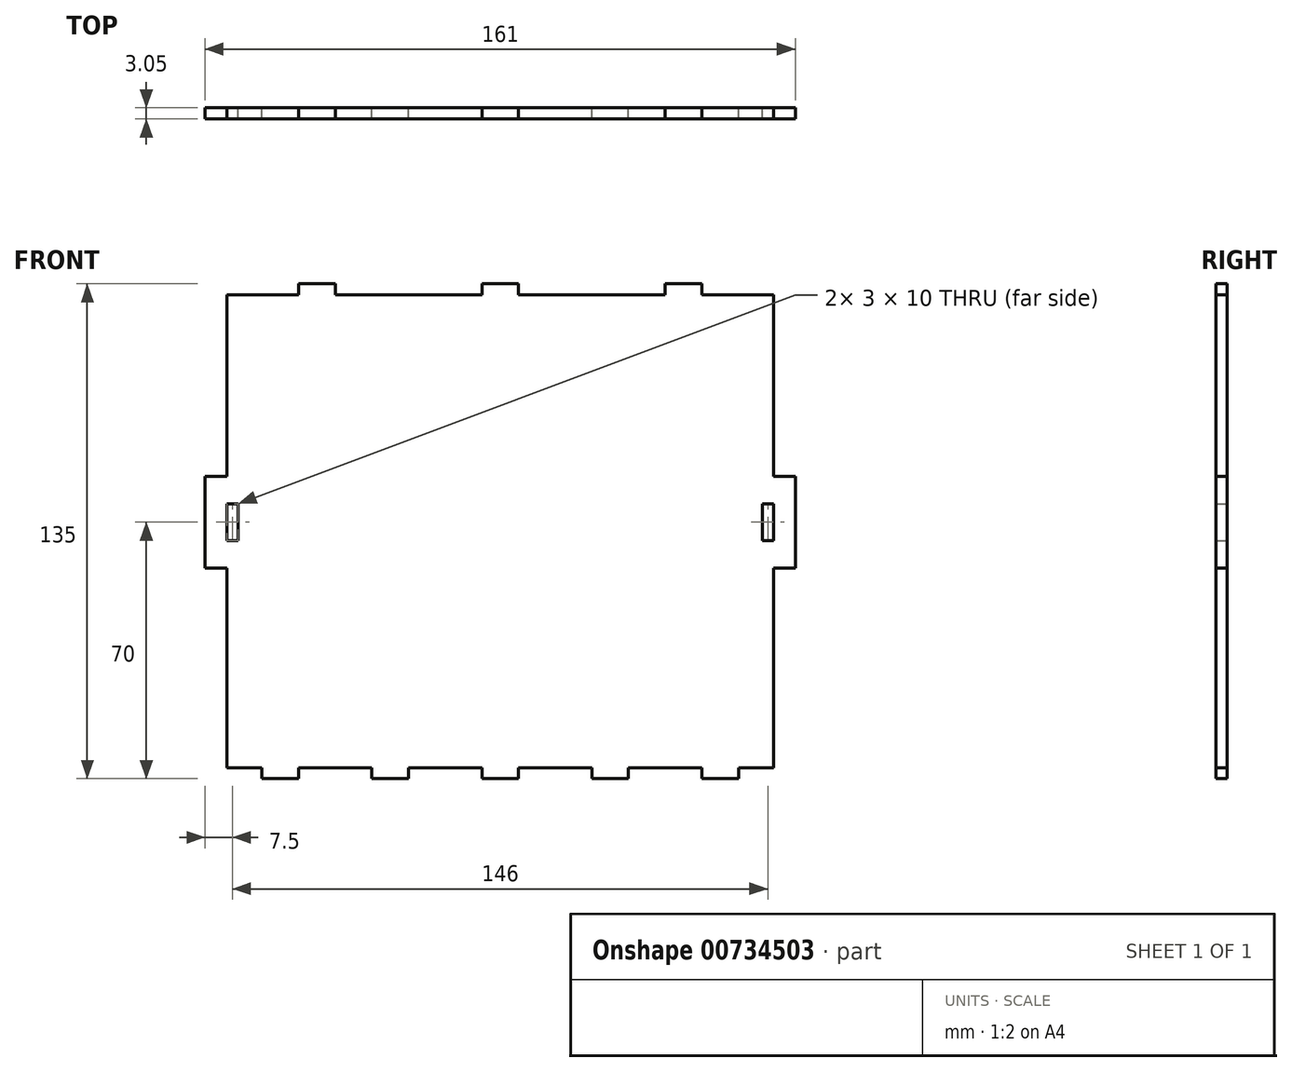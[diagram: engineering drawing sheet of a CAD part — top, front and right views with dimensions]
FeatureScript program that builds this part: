
annotation { "Feature Type Name" : "Feature", "Feature Type Description" : "" }
export const myFeature = defineFeature(function(context is Context, id is Id, definition is map)
    precondition{}
    {
        {
            var Q0;
            Q0=qCreatedBy(makeId("Front.planeOp"),FACE);
            var sketch = newSketch(context, id + "F0", { "sketchPlane" : qUnion([Q0])});
            skLineSegment(sketch, "E0", {"start": v(74.5, 7.5) * mm, "end": v(71.5, 7.5) * mm});
            skLineSegment(sketch, "E1", {"start": v(71.5, 7.5) * mm, "end": v(71.5, -2.5) * mm});
            skLineSegment(sketch, "E2", {"start": v(71.5, -2.5) * mm, "end": v(74.5, -2.5) * mm});
            skLineSegment(sketch, "E3", {"start": v(74.5, -2.5) * mm, "end": v(74.5, 7.5) * mm});
            skLineSegment(sketch, "E4", {"start": v(-74.5, -2.5) * mm, "end": v(-71.5, -2.5) * mm});
            skLineSegment(sketch, "E5", {"start": v(-71.5, -2.5) * mm, "end": v(-71.5, 7.5) * mm});
            skLineSegment(sketch, "E6", {"start": v(-71.5, 7.5) * mm, "end": v(-74.5, 7.5) * mm});
            skLineSegment(sketch, "E7", {"start": v(-74.5, 7.5) * mm, "end": v(-74.5, -2.5) * mm});
            skLineSegment(sketch, "E8", {"start": v(-74.5, 15) * mm, "end": v(-74.5, 64.5) * mm});
            skLineSegment(sketch, "E9", {"start": v(-74.5, 64.5) * mm, "end": v(-55, 64.5) * mm});
            skLineSegment(sketch, "E10", {"start": v(-55, 64.5) * mm, "end": v(-55, 67.5) * mm});
            skLineSegment(sketch, "E11", {"start": v(-55, 67.5) * mm, "end": v(-45, 67.5) * mm});
            skLineSegment(sketch, "E12", {"start": v(-45, 67.5) * mm, "end": v(-45, 64.5) * mm});
            skLineSegment(sketch, "E13", {"start": v(-45, 64.5) * mm, "end": v(-5, 64.5) * mm});
            skLineSegment(sketch, "E14", {"start": v(-5, 64.5) * mm, "end": v(-5, 67.5) * mm});
            skLineSegment(sketch, "E15", {"start": v(-5, 67.5) * mm, "end": v(5, 67.5) * mm});
            skLineSegment(sketch, "E16", {"start": v(5, 67.5) * mm, "end": v(5, 64.5) * mm});
            skLineSegment(sketch, "E17", {"start": v(5, 64.5) * mm, "end": v(45, 64.5) * mm});
            skLineSegment(sketch, "E18", {"start": v(45, 64.5) * mm, "end": v(45, 67.5) * mm});
            skLineSegment(sketch, "E19", {"start": v(45, 67.5) * mm, "end": v(55, 67.5) * mm});
            skLineSegment(sketch, "E20", {"start": v(55, 67.5) * mm, "end": v(55, 64.5) * mm});
            skLineSegment(sketch, "E21", {"start": v(55, 64.5) * mm, "end": v(74.5, 64.5) * mm});
            skLineSegment(sketch, "E22", {"start": v(74.5, 64.5) * mm, "end": v(74.5, 15) * mm});
            skLineSegment(sketch, "E23", {"start": v(74.5, 15) * mm, "end": v(80.5, 15) * mm});
            skLineSegment(sketch, "E24", {"start": v(80.5, 15) * mm, "end": v(80.5, -10) * mm});
            skLineSegment(sketch, "E25", {"start": v(80.5, -10) * mm, "end": v(74.5, -10) * mm});
            skLineSegment(sketch, "E26", {"start": v(74.5, -10) * mm, "end": v(74.5, -64.5) * mm});
            skLineSegment(sketch, "E27", {"start": v(74.5, -64.5) * mm, "end": v(65, -64.5) * mm});
            skLineSegment(sketch, "E28", {"start": v(65, -64.5) * mm, "end": v(65, -67.5) * mm});
            skLineSegment(sketch, "E29", {"start": v(65, -67.5) * mm, "end": v(55, -67.5) * mm});
            skLineSegment(sketch, "E30", {"start": v(55, -67.5) * mm, "end": v(55, -64.5) * mm});
            skLineSegment(sketch, "E31", {"start": v(55, -64.5) * mm, "end": v(35, -64.5) * mm});
            skLineSegment(sketch, "E32", {"start": v(35, -64.5) * mm, "end": v(35, -67.5) * mm});
            skLineSegment(sketch, "E33", {"start": v(35, -67.5) * mm, "end": v(25, -67.5) * mm});
            skLineSegment(sketch, "E34", {"start": v(25, -67.5) * mm, "end": v(25, -64.5) * mm});
            skLineSegment(sketch, "E35", {"start": v(25, -64.5) * mm, "end": v(5, -64.5) * mm});
            skLineSegment(sketch, "E36", {"start": v(5, -64.5) * mm, "end": v(5, -67.5) * mm});
            skLineSegment(sketch, "E37", {"start": v(5, -67.5) * mm, "end": v(-5, -67.5) * mm});
            skLineSegment(sketch, "E38", {"start": v(-5, -67.5) * mm, "end": v(-5, -64.5) * mm});
            skLineSegment(sketch, "E39", {"start": v(-5, -64.5) * mm, "end": v(-25, -64.5) * mm});
            skLineSegment(sketch, "E40", {"start": v(-25, -64.5) * mm, "end": v(-25, -67.5) * mm});
            skLineSegment(sketch, "E41", {"start": v(-25, -67.5) * mm, "end": v(-35, -67.5) * mm});
            skLineSegment(sketch, "E42", {"start": v(-35, -67.5) * mm, "end": v(-35, -64.5) * mm});
            skLineSegment(sketch, "E43", {"start": v(-35, -64.5) * mm, "end": v(-55, -64.5) * mm});
            skLineSegment(sketch, "E44", {"start": v(-55, -64.5) * mm, "end": v(-55, -67.5) * mm});
            skLineSegment(sketch, "E45", {"start": v(-55, -67.5) * mm, "end": v(-65, -67.5) * mm});
            skLineSegment(sketch, "E46", {"start": v(-65, -67.5) * mm, "end": v(-65, -64.5) * mm});
            skLineSegment(sketch, "E47", {"start": v(-65, -64.5) * mm, "end": v(-74.5, -64.5) * mm});
            skLineSegment(sketch, "E48", {"start": v(-74.5, -64.5) * mm, "end": v(-74.5, -10) * mm});
            skLineSegment(sketch, "E49", {"start": v(-74.5, -10) * mm, "end": v(-80.5, -10) * mm});
            skLineSegment(sketch, "E50", {"start": v(-80.5, -10) * mm, "end": v(-80.5, 15) * mm});
            skLineSegment(sketch, "E51", {"start": v(-80.5, 15) * mm, "end": v(-74.5, 15) * mm});
            skSolve(sketch);
        }
        {
            var Q0;
            Q0 = qSketchRegion(id + "F0", true);
            extrude(context, id + "F1", {"entities" : qUnion([Q0]), "depth" : 3.05 * mm, "offsetDistance" : 25.4 * mm});
        }
    });
